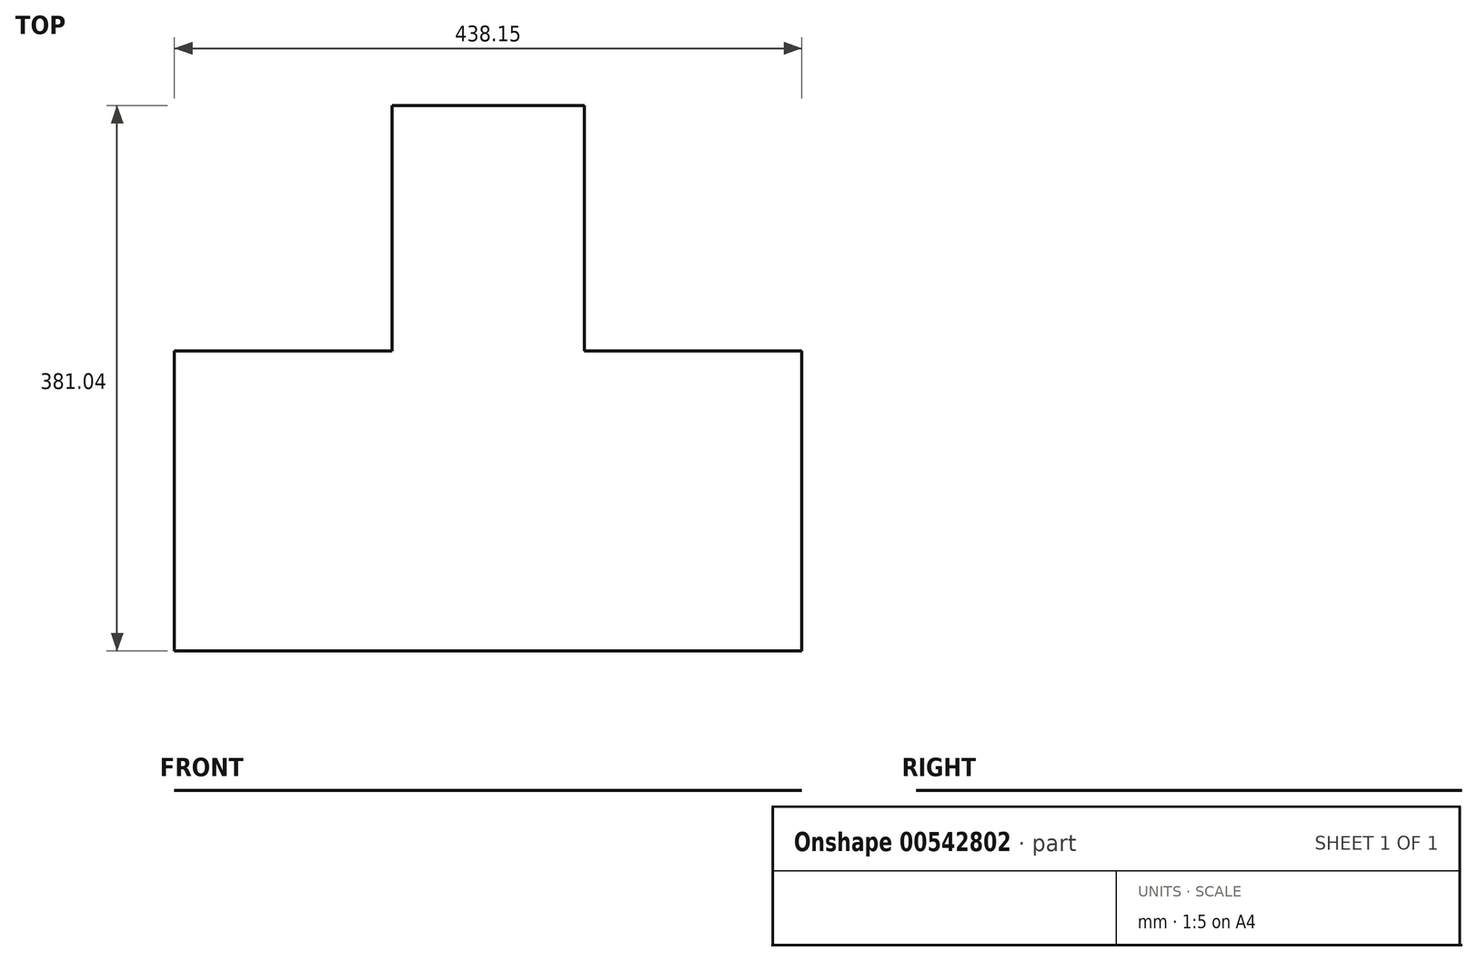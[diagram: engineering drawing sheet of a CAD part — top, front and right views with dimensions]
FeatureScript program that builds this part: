
annotation { "Feature Type Name" : "Feature", "Feature Type Description" : "" }
export const myFeature = defineFeature(function(context is Context, id is Id, definition is map)
    precondition{}
    {
        {
            var Q0;
            Q0=qCreatedBy(makeId("Top.planeOp"),FACE);
            var sketch = newSketch(context, id + "F0", { "sketchPlane" : qUnion([Q0])});
            skLineSegment(sketch, "E0.bottom", {"start": v(-290.6, 189.05) * mm, "end": v(-156.27, 189.05) * mm});
            skLineSegment(sketch, "E0.top", {"start": v(-375.83, -144.5) * mm, "end": v(-71.03, -144.5) * mm});
            skLineSegment(sketch, "E0.left", {"start": v(-375.83, -36.16) * mm, "end": v(-375.83, -144.5) * mm});
            skLineSegment(sketch, "E0.right", {"start": v(-71.03, -36.16) * mm, "end": v(-71.03, -144.5) * mm});
            skLineSegment(sketch, "E1.bottom", {"start": v(-375.83, 189.05) * mm, "end": v(-375.83, 189.05) * mm});
            skLineSegment(sketch, "E1.top", {"start": v(-375.83, -144.5) * mm, "end": v(-375.83, -144.5) * mm});
            skLineSegment(sketch, "E2.left", {"start": v(-290.6, 189.05) * mm, "end": v(-290.6, -36.16) * mm});
            skLineSegment(sketch, "E2.right", {"start": v(-156.27, 189.05) * mm, "end": v(-156.27, -36.16) * mm});
            skLineSegment(sketch, "E3", {"start": v(-290.6, -36.16) * mm, "end": v(-375.83, -36.16) * mm});
            skLineSegment(sketch, "E4", {"start": v(-156.27, -36.16) * mm, "end": v(-71.03, -36.16) * mm});
            skSolve(sketch);
        }
        {
            var Q0;
            Q0=makeQuery(id+"F0.imprint","IMPRINT",FACE,{"disambiguationData":[TD([[makeQuery(id+"F0.imprint","IMPRINT",EDGE,{"derivedFrom":sQuery(id+"F0.wireOp",EDGE,"E0.top")}),1.0]])]});
            extrude(context, id + "F1", {"entities" : qUnion([Q0]), "depth" : 1 / 457.2 * mm, "offsetDistance" : 25.4 * mm});
        }
        {
            var Q0;
            Q0=makeQuery(id+"F1.opExtrude","SWEPT_FACE",FACE,{"disambiguationData":[OSD([sQuery(id+"F0.wireOp",EDGE,"E3")])]});
            var Q1;
            Q1=makeQuery(id+"F1.opExtrude","SWEPT_FACE",FACE,{"disambiguationData":[OSD([sQuery(id+"F0.wireOp",EDGE,"E4")])]});
            extrude(context, id + "F2", {"entities" : qUnion([Q0, Q1]), "operationType" : NewBodyOperationType.ADD, "depth" : 101.23 * mm, "offsetDistance" : 25.4 * mm});
        }
        {
            var Q0;
            {var subQ0=sQuery(id+"F0.wireOp",EDGE,"E0.right");Q0=makeQuery(id+"F2.boolean.opBoolean","MERGE",FACE,{"derivedFrom":[makeQuery(id+"F1.opExtrude","SWEPT_FACE",FACE,{"disambiguationData":[OSD([subQ0])]}),makeQuery(id+"F2.opExtrude","SWEPT_FACE",FACE,{"disambiguationData":[OSD([subQ0,sQuery(id+"F0.wireOp",EDGE,"E4")])]})]});}
            extrude(context, id + "F3", {"entities" : qUnion([Q0]), "operationType" : NewBodyOperationType.ADD, "depth" : 66.67 * mm, "offsetDistance" : 25.4 * mm});
        }
        {
            var Q0;
            {var subQ0=sQuery(id+"F0.wireOp",EDGE,"E0.left");Q0=makeQuery(id+"F2.boolean.opBoolean","MERGE",FACE,{"derivedFrom":[makeQuery(id+"F1.opExtrude","SWEPT_FACE",FACE,{"disambiguationData":[OSD([subQ0])]}),makeQuery(id+"F2.opExtrude","SWEPT_FACE",FACE,{"disambiguationData":[OSD([subQ0,sQuery(id+"F0.wireOp",EDGE,"E3")])]})]});}
            extrude(context, id + "F4", {"entities" : qUnion([Q0]), "operationType" : NewBodyOperationType.ADD, "depth" : 66.67 * mm, "offsetDistance" : 25.4 * mm});
        }
        {
            var Q0;
            Q0=makeQuery(id+"F1.opExtrude","SWEPT_FACE",FACE,{"disambiguationData":[OSD([sQuery(id+"F0.wireOp",EDGE,"E0.bottom")])]});
            extrude(context, id + "F5", {"entities" : qUnion([Q0]), "operationType" : NewBodyOperationType.ADD, "depth" : 47.5 * mm, "offsetDistance" : 25.4 * mm});
        }
    });
